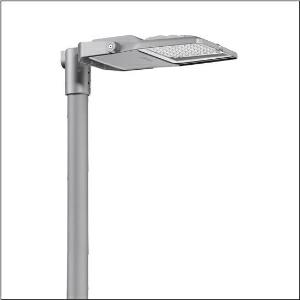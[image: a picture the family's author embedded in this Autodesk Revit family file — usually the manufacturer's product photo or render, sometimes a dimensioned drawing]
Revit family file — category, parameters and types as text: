
# Revit family: floodlight_fl_21_iq_mini___pl64_5xa7771d2e3a_d262
name_source: partatom
category: Lighting Fixtures
units: mm (PartAtom-declared; Revit-internal decimal feet)

## family parameters
Cut with Voids When Loaded = No
Host = Face
Light Source = No
Part Type = Normal
Room Calculation Point = No
Round Connector Dimension = Use Diameter
Shared = No

## types (1)
- --- (1 x LED, 17220 lm, 143 W, 3000K)
    Apparent Load = 143 VA
    CIE Flux Codes = 28 80 98 100 100
    Color Rendering = 70
    Color Temperature = 3000K
    Default Elevation = 1800 mm
    Description = Floodlight FL 21 iQ mini, floodlight, primary light control with lens, of PMMA, primary optical cover: protective disc, of toughened safety glass, transparent, light distribution: PL64, light emission: direct distribution, installation type: surface-mounted, LED, High Power LED, rated luminous flux: 17.220lm, luminous efficacy: 120lm/W, light colour: 730, colour temperature: 3000K, control: Auto-Match, Temp-Guard, Lumen-Switch, Night-Set, Smart-Wire, Light-Fading, Desk-Remote (wireless, voltage-free reading and setting of iQ features in the workshop via application-optimized NFC function/RFID function), optimised constant luminous flux control (CLO 2.0), with terminal, 6-pole, mains connection: 220..240V, AC, 50/60Hz, start of lifetime: 143W, end of service life: 152W, reduction: 61W, luminaire housing, of diecast aluminium, powder-coated, Siteco® metallic grey (DB 702S), corrosivity category C5 mid according to DIN EN ISO 12944, sealing non-destructively replaceable, please order mast flange separately, mast bracket, of steel, galvanised, powder-coated, Siteco® metallic grey (DB 702S), protection rating (complete): IP66, insulation class (complete): insulation class II (safety insulation), certification: CE, ENEC, VDE, protection symbol: D, impact resistance: IK08, permissible operating ambient temperature: -40..+40°C, permissible operating ambient temperature for outdoor applications: -40..+50°C, standard: DIN EN 12944, LABS conformity tested according to VDMA 24364:2018-05, packaging unit: 1 piece

Light Distribution: PL64
    Height = 70 mm
    Lamp = 1 x LED
    Lamp Light Flux = 17220 lm
    Lamp Power = 143 W
    Lamp count = 1
    Length = 485 mm
    Luminous efficacy = 120 lm/W
    Manufacturer = Siteco
    ModVariant = No
    Model = 5XA7771D2E3A
    Number of Poles = 1
    OnlyDefault = Yes
    Power Factor = 1
    Product Name = Floodlight FL 21 iQ mini | PL64
    Product group = floodlight | pylon annexe
    ProductGroupID = 6200
    Protection Class = Protection class II
    Protection Degree = IP 66
    RLX_Detail_Level = 1
    RLX_Emergency_Light_Flux = 0 lm
    RLX_Emergency_Type = 0
    RLX_Emergency_Type_DB = No
    RlxData = <blob elided: 101493 chars, md5=57bcea2f>
    Socket = socket
    Standby Power = 0 W
    System Light Flux = 17220 lm
    System Power = 143 W
    Type Comments = factory setting: luminous flux: 100 % | dim-lin: 254 | 730 mA
    Type Image = l_1007125.jpg
    URL = http://relux.com
    VarID = @adj_116219
    Voltage = 0 V
    Weight = 0.00 kg
    Width = 337 mm

## geometry (parser evidence)
native form markers: Blend x4, Sweep x13
no freeform markers — native parametric forms only
